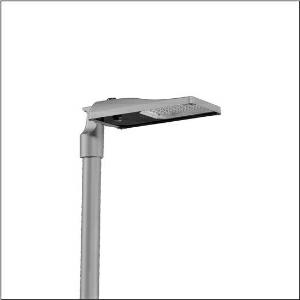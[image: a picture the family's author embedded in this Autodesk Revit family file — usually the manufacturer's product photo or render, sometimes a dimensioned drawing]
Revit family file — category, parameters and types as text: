
# Revit family: streetlight_sl_31_mini___st1_0a_5xh6d3at08ha_0bc3
name_source: partatom
category: Lighting Fixtures
units: mm (PartAtom-declared; Revit-internal decimal feet)

## family parameters
Cut with Voids When Loaded = No
Host = Face
Light Source = No
Part Type = Normal
Room Calculation Point = No
Round Connector Dimension = Use Diameter
Shared = No

## types (1)
- --- (1 x LED, 9230 lm, 68.3 W, 3000K)
    Apparent Load = 68 VA
    CIE Flux Codes = 37 72 97 100 100
    Color Rendering = 70
    Color Temperature = 3000K
    Default Elevation = 1800 mm
    Description = Streetlight SL 31 mini D4i mast luminaire for post-top, side-entry; light control with lens of PMMA; light distribution: ST1.0a, direct asymmetric distribution, for standard-compliant lighting for roads and squares; LED: luminous flux: 9.230lm, light colour: 730, colour temperature: 3000K; luminous efficacy: 135,1lm/W; control: pre-setting: logarithmic dimming characteristic, flexible luminous flux parameterisation, time-dependent luminous flux control, constant luminous flux control, power reduction, intelligent temperature release in ECG and LED module, overheat protection; luminaire housing, of diecast aluminium, SITECO metallic grey (DB 702S), corrosivity category C5 high according to DIN EN ISO 12944; cover of toughened safety glass, transparent, opened without tools; mast flange of diecast aluminium, SITECO metallic grey (DB 702S), spigot size: 76/60mm, mast flange included unmounted; cable length: 8,5m, connection cable pre-assembled; mains connection: 220..240V, AC, 50/60Hz; power consumption (at start of service life): 68,3W / (at end of service life): 74,5W / (with reduced operation 50%): 29,5W; protection rating (complete): IP66; insulation class (complete): insulation class II (safety insulation); impact resistance: IK09; certification: CE, ENEC, ENEC+, VDE, UKCA, ZD4i; permissible operating ambient temperature for outdoor applications: -40..+50°C; packaging unit: 1 piece

Light Distribution: ST1.0a
    Height = 76 mm
    Lamp = 1 x LED
    Lamp Light Flux = 9230 lm
    Lamp Power = 68.3 W
    Lamp count = 1
    Length = 547 mm
    Luminous efficacy = 135 lm/W
    Manufacturer = Siteco
    ModVariant = No
    Model = 5XH6D3AT08HA
    Number of Poles = 1
    OnlyDefault = Yes
    Power Factor = 1
    Product Name = Streetlight SL 31 mini | ST1.0a
    Product group = mast luminaire | pylon top
    ProductGroupID = 6100
    Protection Class = Protection class II
    Protection Degree = IP 66
    RLX_Detail_Level = 1
    RLX_Emergency_Light_Flux = 0 lm
    RLX_Emergency_Type = 0
    RLX_Emergency_Type_DB = No
    RlxData = <blob elided: 24285 chars, md5=2b1cf12e>
    Socket = socket
    Standby Power = 0 W
    System Light Flux = 9230 lm
    System Power = 68 W
    Type Comments = factory setting: luminous flux: 100 % | dim-lin: 254 | 692 mA
    Type Image = l_1300332.jpg
    URL = http://relux.com
    VarID = @adj_020245
    Voltage = 0 V
    Weight = 0.00 kg
    Width = 265 mm

## geometry (parser evidence)
native form markers: Blend x4, Sweep x11
no freeform markers — native parametric forms only
